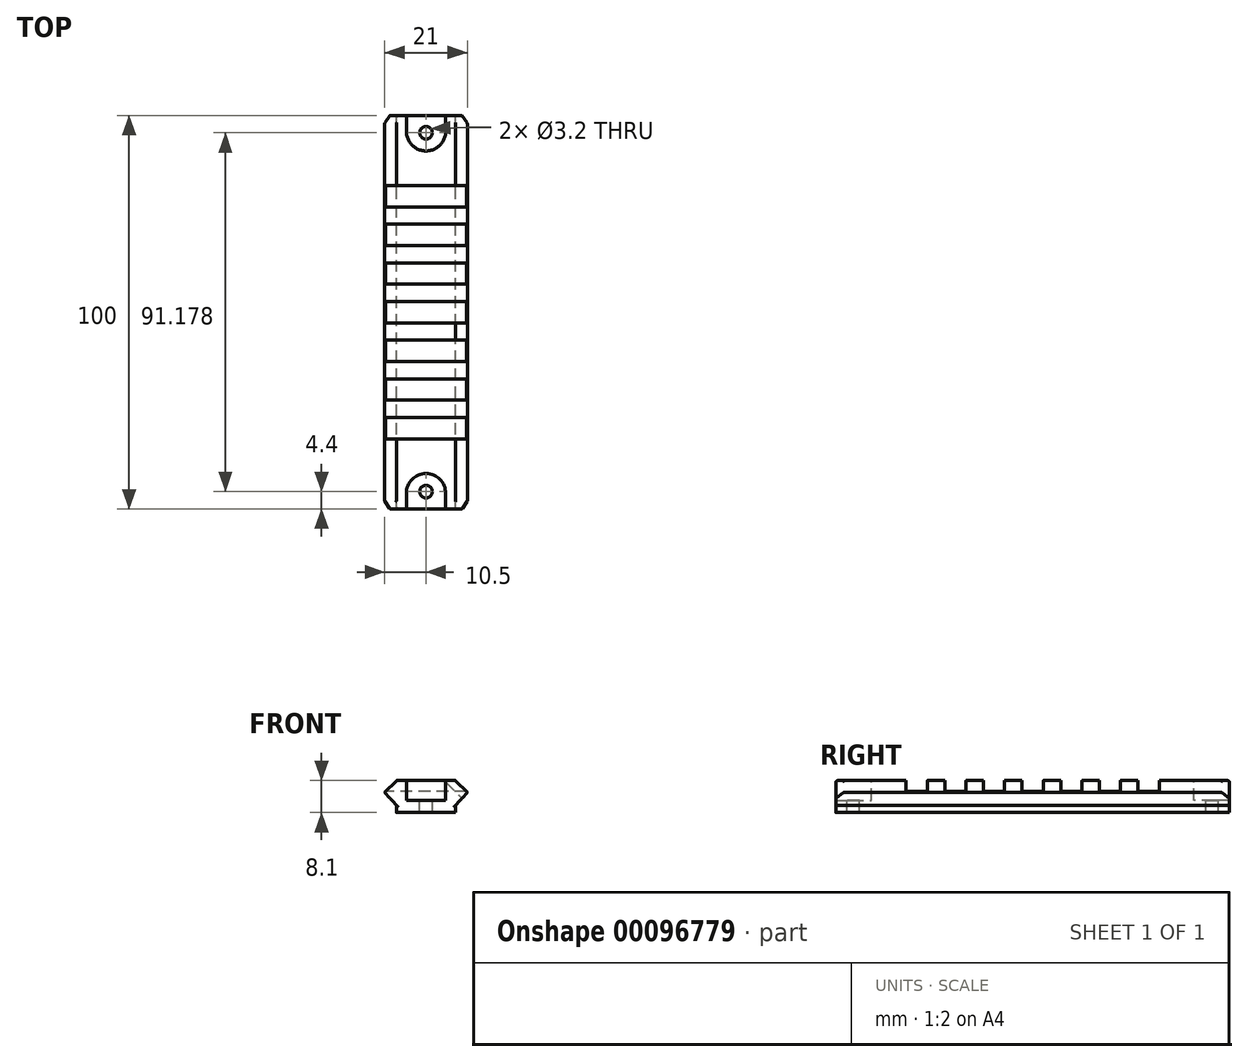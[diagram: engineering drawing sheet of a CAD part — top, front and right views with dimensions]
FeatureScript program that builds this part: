
annotation { "Feature Type Name" : "Feature", "Feature Type Description" : "" }
export const myFeature = defineFeature(function(context is Context, id is Id, definition is map)
    precondition{}
    {
        {
            var Q0;
            Q0=qCreatedBy(makeId("Front.planeOp"),FACE);
            var sketch = newSketch(context, id + "F0", { "sketchPlane" : qUnion([Q0])});
            skPoint(sketch, "E0", {"position": v(7.5, 0) * mm});
            skPoint(sketch, "E1", {"position": v(-7.5, 0) * mm});
            skPoint(sketch, "E2", {"position": v(0, 3.3) * mm});
            skPoint(sketch, "E3", {"position": v(0, -4.8) * mm});
            skLineSegment(sketch, "E4", {"start": v(7.5, -4.8) * mm, "end": v(-7.5, -4.8) * mm});
            skLineSegment(sketch, "E5", {"start": v(7.5, -4.8) * mm, "end": v(7.5, -3) * mm});
            skLineSegment(sketch, "E6", {"start": v(-7.5, -3) * mm, "end": v(-7.5, -4.8) * mm});
            skLineSegment(sketch, "E7", {"start": v(-7.5, -3) * mm, "end": v(-10.5, 0.3) * mm});
            skLineSegment(sketch, "E8", {"start": v(7.5, -3) * mm, "end": v(10.5, 0.3) * mm});
            skPoint(sketch, "E9", {"position": v(7.5, 3.3) * mm});
            skPoint(sketch, "E10", {"position": v(-7.5, 3.3) * mm});
            skLineSegment(sketch, "E11", {"start": v(-10.5, 0.3) * mm, "end": v(-7.5, 3.3) * mm});
            skLineSegment(sketch, "E12", {"start": v(10.5, 0.3) * mm, "end": v(7.5, 3.3) * mm});
            skLineSegment(sketch, "E13", {"start": v(-7.5, 3.3) * mm, "end": v(7.5, 3.3) * mm});
            skSolve(sketch);
        }
        {
            var Q0;
            Q0=qSketchRegion(id+"F0",true);
            extrude(context, id + "F1", {"entities" : qUnion([Q0]), "endBound" : BoundingType.SYMMETRIC, "depth" : 100 * mm});
        }
        {
            var Q0;
            Q0=makeQuery(id+"F1.opExtrude","SWEPT_FACE",FACE,{"disambiguationData":[OSD([sQuery(id+"F0.wireOp",EDGE,"E13")])]});
            var sketch = newSketch(context, id + "F2", { "sketchPlane" : qUnion([Q0])});
            skPoint(sketch, "E14", {"position": v(0, 2.7) * mm});
            skPoint(sketch, "E15", {"position": v(0, -2.7) * mm});
            skLineSegment(sketch, "E16", {"start": v(-14, -2.7) * mm, "end": v(14, -2.7) * mm});
            skLineSegment(sketch, "E17", {"start": v(14, -2.7) * mm, "end": v(14, 2.7) * mm});
            skLineSegment(sketch, "E18", {"start": v(14, 2.7) * mm, "end": v(-14, 2.7) * mm});
            skLineSegment(sketch, "E19", {"start": v(-14, -2.7) * mm, "end": v(-14, 2.7) * mm});
            skLineSegment(sketch, "E20", {"start": v(0, 50) * mm, "end": v(0, 35) * mm});
            skPoint(sketch, "E20.endSnap0", {"position": v(0, 50) * mm});
            skLineSegment(sketch, "E21.0.1.0", {"start": v(-14, 7.12) * mm, "end": v(-14.1, 12.52) * mm});
            skLineSegment(sketch, "E21.0.1.1", {"start": v(14.12, 12.52) * mm, "end": v(-14.1, 12.52) * mm});
            skLineSegment(sketch, "E21.0.1.2", {"start": v(-14, 7.12) * mm, "end": v(14.12, 7.12) * mm});
            skLineSegment(sketch, "E21.0.1.3", {"start": v(14.12, 7.12) * mm, "end": v(14.12, 12.52) * mm});
            skLineSegment(sketch, "E21.0.2.0", {"start": v(-13.81, 16.94) * mm, "end": v(-13.81, 22.34) * mm});
            skLineSegment(sketch, "E21.0.2.1", {"start": v(14.52, 22.34) * mm, "end": v(-13.81, 22.34) * mm});
            skLineSegment(sketch, "E21.0.2.2", {"start": v(-13.81, 16.94) * mm, "end": v(14.52, 16.94) * mm});
            skLineSegment(sketch, "E21.0.2.3", {"start": v(14.52, 16.94) * mm, "end": v(14.52, 22.34) * mm});
            skLineSegment(sketch, "E21.0.3.0", {"start": v(-14.12, 26.76) * mm, "end": v(-14.12, 32.16) * mm});
            skLineSegment(sketch, "E21.0.3.1", {"start": v(14.7, 32.16) * mm, "end": v(-14.12, 32.16) * mm});
            skLineSegment(sketch, "E21.0.3.2", {"start": v(-14.12, 26.76) * mm, "end": v(14.7, 26.76) * mm});
            skLineSegment(sketch, "E21.0.3.3", {"start": v(14.7, 26.76) * mm, "end": v(14.7, 32.16) * mm});
            skLineSegment(sketch, "E21.direction2", {"start": v(-14, -2.7) * mm, "end": v(-14, 7.12) * mm, "construction": true});
            skLineSegment(sketch, "E22.0.1.0", {"start": v(-13.9, -12.52) * mm, "end": v(14.62, -12.52) * mm});
            skLineSegment(sketch, "E22.0.1.1", {"start": v(-13.9, -12.52) * mm, "end": v(-13.9, -7.12) * mm});
            skLineSegment(sketch, "E22.0.1.2", {"start": v(14.62, -7.12) * mm, "end": v(-13.9, -7.12) * mm});
            skLineSegment(sketch, "E22.0.1.3", {"start": v(14.62, -12.52) * mm, "end": v(14.62, -7.12) * mm});
            skLineSegment(sketch, "E22.0.2.0", {"start": v(-14.68, -22.34) * mm, "end": v(14.93, -22.34) * mm});
            skLineSegment(sketch, "E22.0.2.1", {"start": v(-14.68, -22.34) * mm, "end": v(-14.68, -16.94) * mm});
            skLineSegment(sketch, "E22.0.2.2", {"start": v(14.93, -16.94) * mm, "end": v(-14.68, -16.94) * mm});
            skLineSegment(sketch, "E22.0.2.3", {"start": v(14.93, -22.34) * mm, "end": v(14.93, -16.94) * mm});
            skLineSegment(sketch, "E22.0.3.0", {"start": v(-14.78, -32.16) * mm, "end": v(15.13, -32.16) * mm});
            skLineSegment(sketch, "E22.0.3.1", {"start": v(-14.78, -32.16) * mm, "end": v(-14.78, -26.76) * mm});
            skLineSegment(sketch, "E22.0.3.2", {"start": v(15.13, -26.76) * mm, "end": v(-14.78, -26.76) * mm});
            skLineSegment(sketch, "E22.0.3.3", {"start": v(15.13, -32.16) * mm, "end": v(15.13, -26.76) * mm});
            skLineSegment(sketch, "E22.direction2", {"start": v(-14, -2.7) * mm, "end": v(-13.9, -12.52) * mm, "construction": true});
            skSolve(sketch);
        }
        {
            var Q0;
            Q0=qSketchRegion(id+"F2",true);
            extrude(context, id + "F3", {"entities" : qUnion([Q0]), "operationType" : NewBodyOperationType.REMOVE, "oppositeDirection" : true, "depth" : 2.8 * mm});
        }
        {
            var Q0;
            Q0=qCreatedBy(makeId("Top.planeOp"),FACE);
            var sketch = newSketch(context, id + "F4", { "sketchPlane" : qUnion([Q0])});
            skPoint(sketch, "E23", {"position": v(0, -50) * mm});
            skPoint(sketch, "E24", {"position": v(0, -48) * mm});
            skPoint(sketch, "E25", {"position": v(-11, -48.94) * mm});
            skPoint(sketch, "E26", {"position": v(-5, -48.94) * mm});
            skPoint(sketch, "E27", {"position": v(5, -48.94) * mm});
            skPoint(sketch, "E28", {"position": v(-5, -50) * mm});
            skPoint(sketch, "E29", {"position": v(5, -50) * mm});
            skLineSegment(sketch, "E30", {"start": v(-5, -48) * mm, "end": v(-5, -50) * mm});
            skLineSegment(sketch, "E31", {"start": v(-5, -48) * mm, "end": v(-5, -43) * mm});
            skLineSegment(sketch, "E32", {"start": v(5, -50) * mm, "end": v(5, -48) * mm});
            skLineSegment(sketch, "E33", {"start": v(5, -48) * mm, "end": v(5, -43) * mm});
            skArc(sketch, "E34", {"start": v(5, -43) * mm, "mid": v(0, -38) * mm, "end": v(-5, -43) * mm});
            skArc(sketch, "E35.MirrorCS", {"start": v(5, 43) * mm, "mid": v(0, 38) * mm, "end": v(-5, 43) * mm});
            skLineSegment(sketch, "E36.MirrorCS", {"start": v(-5, 48) * mm, "end": v(-5, 43) * mm});
            skLineSegment(sketch, "E37.MirrorCS", {"start": v(5, 48) * mm, "end": v(5, 43) * mm});
            skLineSegment(sketch, "E38.MirrorCS", {"start": v(5, 50) * mm, "end": v(5, 48) * mm});
            skLineSegment(sketch, "E39.MirrorCS", {"start": v(-5, 48) * mm, "end": v(-5, 50) * mm});
            skSolve(sketch);
        }
        {
            var Q0;
            {var subQ0=sQuery(id+"F0.wireOp",EDGE,"E13");Q0=makeQuery(id+"F3.boolean.opBoolean","SPLIT",FACE,{"disambiguationData":[TD([makeQuery(id+"F3.opExtrude","SWEPT_FACE",FACE,{"disambiguationData":[OSD([sQuery(id+"F2.wireOp",EDGE,"E22.0.3.0")])]})])],"derivedFrom":makeQuery(id+"F1.opExtrude","SWEPT_FACE",FACE,{"disambiguationData":[OSD([subQ0])]})});}
            var sketch = newSketch(context, id + "F5", { "sketchPlane" : qUnion([Q0])});
            skPoint(sketch, "E40", {"position": v(0, -50) * mm});
            skPoint(sketch, "E41", {"position": v(0, -48) * mm});
            skPoint(sketch, "E42", {"position": v(-11, -48.94) * mm});
            skPoint(sketch, "E43", {"position": v(-5, -48.94) * mm});
            skPoint(sketch, "E44", {"position": v(5, -48.94) * mm});
            skPoint(sketch, "E45", {"position": v(-5, -50) * mm});
            skPoint(sketch, "E46", {"position": v(5, -50) * mm});
            skLineSegment(sketch, "E47", {"start": v(-5, -48) * mm, "end": v(-5, -50) * mm});
            skLineSegment(sketch, "E48", {"start": v(-5, -48) * mm, "end": v(-5, -46) * mm});
            skLineSegment(sketch, "E49", {"start": v(5, -50) * mm, "end": v(5, -48) * mm});
            skLineSegment(sketch, "E50", {"start": v(5, -48) * mm, "end": v(5, -46) * mm});
            skArc(sketch, "E51", {"start": v(5, -46) * mm, "mid": v(0, -41) * mm, "end": v(-5, -46) * mm});
            skArc(sketch, "E52.MirrorCS", {"start": v(5, 46) * mm, "mid": v(0, 40.98) * mm, "end": v(-5, 46) * mm});
            skLineSegment(sketch, "E53.MirrorCS", {"start": v(-5, 48) * mm, "end": v(-5, 46) * mm});
            skLineSegment(sketch, "E54.MirrorCS", {"start": v(5, 48) * mm, "end": v(5, 46) * mm});
            skLineSegment(sketch, "E55.MirrorCS", {"start": v(5, 50) * mm, "end": v(5, 48) * mm});
            skLineSegment(sketch, "E56.MirrorCS", {"start": v(-5, 48) * mm, "end": v(-5, 50) * mm});
            skLineSegment(sketch, "E57", {"start": v(-5, -50) * mm, "end": v(5, -50) * mm});
            skLineSegment(sketch, "E58", {"start": v(-5, 50) * mm, "end": v(5, 50) * mm});
            skSolve(sketch);
        }
        {
            var Q0;
            Q0=qSketchRegion(id+"F5",true);
            extrude(context, id + "F6", {"entities" : qUnion([Q0]), "operationType" : NewBodyOperationType.REMOVE, "oppositeDirection" : true, "depth" : 5 * mm});
        }
        {
            var Q0;
            Q0=makeQuery(id+"F6.boolean.opBoolean","COPY",FACE,{"derivedFrom":makeQuery(id+"F6.opExtrude","CAP_FACE",FACE,{"disambiguationData":[OSD([sQuery(id+"F5.wireOp",EDGE,"E47"),sQuery(id+"F5.wireOp",EDGE,"E48"),sQuery(id+"F5.wireOp",EDGE,"E49"),sQuery(id+"F5.wireOp",EDGE,"E50"),sQuery(id+"F5.wireOp",EDGE,"E51"),sQuery(id+"F5.wireOp",EDGE,"E57")])],"isStart":false})});
            var sketch = newSketch(context, id + "F7", { "sketchPlane" : qUnion([Q0])});
            skCircle(sketch, "E59", {"center": v(0, -45.6) * mm, "radius": 1.6 * mm});
            skCircle(sketch, "E60", {"center": v(0, 45.58) * mm, "radius": 1.6 * mm});
            skSolve(sketch);
        }
        {
            var Q0;
            Q0=qSketchRegion(id+"F7",true);
            extrude(context, id + "F8", {"entities" : qUnion([Q0]), "operationType" : NewBodyOperationType.REMOVE, "endBound" : BoundingType.THROUGH_ALL, "oppositeDirection" : true, "depth" : 25 * mm});
        }
        {
            var Q0;
            Q0=makeQuery(id+"F1.opExtrude","CAP_EDGE",EDGE,{"disambiguationData":[OSD([sQuery(id+"F0.wireOp",EDGE,"E12")])],"isStart":true});
            var Q1;
            Q1=makeQuery(id+"F1.opExtrude","CAP_EDGE",EDGE,{"disambiguationData":[OSD([sQuery(id+"F0.wireOp",EDGE,"E11")])],"isStart":true});
            var Q2;
            Q2=makeQuery(id+"F1.opExtrude","CAP_EDGE",EDGE,{"disambiguationData":[OSD([sQuery(id+"F0.wireOp",EDGE,"E12")])],"isStart":false});
            var Q3;
            Q3=makeQuery(id+"F1.opExtrude","CAP_EDGE",EDGE,{"disambiguationData":[OSD([sQuery(id+"F0.wireOp",EDGE,"E11")])],"isStart":false});
            chamfer(context, id + "F9", {"entities" : qUnion([Q0, Q1, Q2, Q3]), "width" : 2 * mm, "tangentPropagation" : true});
        }
        {
            var Q0;
            {var subQ0=sQuery(id+"F0.wireOp",EDGE,"E11");var subQ1=sQuery(id+"F0.wireOp",EDGE,"E13");Q0=makeQuery(id+"F3.boolean.opBoolean","SPLIT",EDGE,{"disambiguationData":[TD([makeQuery(id+"F3.opExtrude","SWEPT_FACE",FACE,{"disambiguationData":[OSD([sQuery(id+"F2.wireOp",EDGE,"E21.0.2.1")])]})])],"derivedFrom":makeQuery(id+"F1.opExtrude","SWEPT_EDGE",EDGE,{"disambiguationData":[OSD([subQ0,subQ1])]})});}
            var Q1;
            {var subQ0=sQuery(id+"F0.wireOp",EDGE,"E11");var subQ1=sQuery(id+"F0.wireOp",EDGE,"E13");Q1=makeQuery(id+"F3.boolean.opBoolean","SPLIT",EDGE,{"disambiguationData":[TD([makeQuery(id+"F3.opExtrude","SWEPT_FACE",FACE,{"disambiguationData":[OSD([sQuery(id+"F2.wireOp",EDGE,"E21.0.1.1")])]})])],"derivedFrom":makeQuery(id+"F1.opExtrude","SWEPT_EDGE",EDGE,{"disambiguationData":[OSD([subQ0,subQ1])]})});}
            var Q2;
            {var subQ0=sQuery(id+"F0.wireOp",EDGE,"E11");var subQ1=sQuery(id+"F0.wireOp",EDGE,"E13");Q2=makeQuery(id+"F3.boolean.opBoolean","SPLIT",EDGE,{"disambiguationData":[TD([makeQuery(id+"F3.opExtrude","SWEPT_FACE",FACE,{"disambiguationData":[OSD([sQuery(id+"F2.wireOp",EDGE,"E18")])]})])],"derivedFrom":makeQuery(id+"F1.opExtrude","SWEPT_EDGE",EDGE,{"disambiguationData":[OSD([subQ0,subQ1])]})});}
            var Q3;
            {var subQ0=sQuery(id+"F0.wireOp",EDGE,"E11");var subQ1=sQuery(id+"F0.wireOp",EDGE,"E13");Q3=makeQuery(id+"F3.boolean.opBoolean","SPLIT",EDGE,{"disambiguationData":[TD([makeQuery(id+"F3.opExtrude","SWEPT_FACE",FACE,{"disambiguationData":[OSD([sQuery(id+"F2.wireOp",EDGE,"E16")])]})])],"derivedFrom":makeQuery(id+"F1.opExtrude","SWEPT_EDGE",EDGE,{"disambiguationData":[OSD([subQ0,subQ1])]})});}
            var Q4;
            {var subQ0=sQuery(id+"F0.wireOp",EDGE,"E11");var subQ1=sQuery(id+"F0.wireOp",EDGE,"E13");Q4=makeQuery(id+"F3.boolean.opBoolean","SPLIT",EDGE,{"disambiguationData":[TD([makeQuery(id+"F3.opExtrude","SWEPT_FACE",FACE,{"disambiguationData":[OSD([sQuery(id+"F2.wireOp",EDGE,"E22.0.1.0")])]})])],"derivedFrom":makeQuery(id+"F1.opExtrude","SWEPT_EDGE",EDGE,{"disambiguationData":[OSD([subQ0,subQ1])]})});}
            var Q5;
            {var subQ0=sQuery(id+"F0.wireOp",EDGE,"E11");var subQ1=sQuery(id+"F0.wireOp",EDGE,"E13");Q5=makeQuery(id+"F3.boolean.opBoolean","SPLIT",EDGE,{"disambiguationData":[TD([makeQuery(id+"F3.opExtrude","SWEPT_FACE",FACE,{"disambiguationData":[OSD([sQuery(id+"F2.wireOp",EDGE,"E22.0.2.0")])]})])],"derivedFrom":makeQuery(id+"F1.opExtrude","SWEPT_EDGE",EDGE,{"disambiguationData":[OSD([subQ0,subQ1])]})});}
            var Q6;
            {var subQ0=sQuery(id+"F0.wireOp",EDGE,"E12");var subQ1=sQuery(id+"F0.wireOp",EDGE,"E13");Q6=makeQuery(id+"F3.boolean.opBoolean","SPLIT",EDGE,{"disambiguationData":[TD([makeQuery(id+"F3.opExtrude","SWEPT_FACE",FACE,{"disambiguationData":[OSD([sQuery(id+"F2.wireOp",EDGE,"E22.0.2.0")])]})])],"derivedFrom":makeQuery(id+"F1.opExtrude","SWEPT_EDGE",EDGE,{"disambiguationData":[OSD([subQ0,subQ1])]})});}
            var Q7;
            {var subQ0=sQuery(id+"F0.wireOp",EDGE,"E12");var subQ1=sQuery(id+"F0.wireOp",EDGE,"E13");Q7=makeQuery(id+"F3.boolean.opBoolean","SPLIT",EDGE,{"disambiguationData":[TD([makeQuery(id+"F3.opExtrude","SWEPT_FACE",FACE,{"disambiguationData":[OSD([sQuery(id+"F2.wireOp",EDGE,"E22.0.1.0")])]})])],"derivedFrom":makeQuery(id+"F1.opExtrude","SWEPT_EDGE",EDGE,{"disambiguationData":[OSD([subQ0,subQ1])]})});}
            var Q8;
            {var subQ0=sQuery(id+"F0.wireOp",EDGE,"E12");var subQ1=sQuery(id+"F0.wireOp",EDGE,"E13");Q8=makeQuery(id+"F3.boolean.opBoolean","SPLIT",EDGE,{"disambiguationData":[TD([makeQuery(id+"F3.opExtrude","SWEPT_FACE",FACE,{"disambiguationData":[OSD([sQuery(id+"F2.wireOp",EDGE,"E18")])]})])],"derivedFrom":makeQuery(id+"F1.opExtrude","SWEPT_EDGE",EDGE,{"disambiguationData":[OSD([subQ0,subQ1])]})});}
            var Q9;
            {var subQ0=sQuery(id+"F0.wireOp",EDGE,"E12");var subQ1=sQuery(id+"F0.wireOp",EDGE,"E13");Q9=makeQuery(id+"F3.boolean.opBoolean","SPLIT",EDGE,{"disambiguationData":[TD([makeQuery(id+"F3.opExtrude","SWEPT_FACE",FACE,{"disambiguationData":[OSD([sQuery(id+"F2.wireOp",EDGE,"E21.0.1.1")])]})])],"derivedFrom":makeQuery(id+"F1.opExtrude","SWEPT_EDGE",EDGE,{"disambiguationData":[OSD([subQ0,subQ1])]})});}
            var Q10;
            {var subQ0=sQuery(id+"F0.wireOp",EDGE,"E12");var subQ1=sQuery(id+"F0.wireOp",EDGE,"E13");Q10=makeQuery(id+"F3.boolean.opBoolean","SPLIT",EDGE,{"disambiguationData":[TD([makeQuery(id+"F3.opExtrude","SWEPT_FACE",FACE,{"disambiguationData":[OSD([sQuery(id+"F2.wireOp",EDGE,"E21.0.2.1")])]})])],"derivedFrom":makeQuery(id+"F1.opExtrude","SWEPT_EDGE",EDGE,{"disambiguationData":[OSD([subQ0,subQ1])]})});}
            var Q11;
            {var subQ0=sQuery(id+"F0.wireOp",EDGE,"E13");var subQ2=sQuery(id+"F0.wireOp",EDGE,"E11");Q11=makeQuery(id+"F9.opChamfer","BLEND_EDGE",EDGE,{"blendedFrom":[makeQuery(id+"F1.opExtrude","CAP_EDGE",EDGE,{"disambiguationData":[OSD([subQ2])],"isStart":true}),makeQuery(id+"F3.boolean.opBoolean","SPLIT",FACE,{"disambiguationData":[TD([makeQuery(id+"F3.opExtrude","SWEPT_FACE",FACE,{"disambiguationData":[OSD([sQuery(id+"F2.wireOp",EDGE,"E21.0.3.1")])]})])],"derivedFrom":makeQuery(id+"F1.opExtrude","SWEPT_FACE",FACE,{"disambiguationData":[OSD([subQ0])]})})],"blendedInto":[makeQuery(id+"F3.boolean.opBoolean","SPLIT",FACE,{"disambiguationData":[TD([makeQuery(id+"F3.opExtrude","SWEPT_FACE",FACE,{"disambiguationData":[OSD([sQuery(id+"F2.wireOp",EDGE,"E21.0.3.1")])]})])],"derivedFrom":makeQuery(id+"F1.opExtrude","SWEPT_FACE",FACE,{"disambiguationData":[OSD([subQ0])]})})]});}
            var Q12;
            {var subQ0=sQuery(id+"F0.wireOp",EDGE,"E11");Q12=makeQuery(id+"F9.opChamfer","BLEND_EDGE",EDGE,{"blendedFrom":[makeQuery(id+"F1.opExtrude","CAP_EDGE",EDGE,{"disambiguationData":[OSD([subQ0])],"isStart":true}),makeQuery(id+"F1.opExtrude","CAP_FACE",FACE,{"disambiguationData":[OSD([sQuery(id+"F0.wireOp",EDGE,"E4"),sQuery(id+"F0.wireOp",EDGE,"E5"),sQuery(id+"F0.wireOp",EDGE,"E6"),sQuery(id+"F0.wireOp",EDGE,"E7"),sQuery(id+"F0.wireOp",EDGE,"E8"),subQ0,sQuery(id+"F0.wireOp",EDGE,"E12"),sQuery(id+"F0.wireOp",EDGE,"E13")])],"isStart":true})],"blendedInto":[makeQuery(id+"F1.opExtrude","CAP_FACE",FACE,{"disambiguationData":[OSD([sQuery(id+"F0.wireOp",EDGE,"E4"),sQuery(id+"F0.wireOp",EDGE,"E5"),sQuery(id+"F0.wireOp",EDGE,"E6"),sQuery(id+"F0.wireOp",EDGE,"E7"),sQuery(id+"F0.wireOp",EDGE,"E8"),subQ0,sQuery(id+"F0.wireOp",EDGE,"E12"),sQuery(id+"F0.wireOp",EDGE,"E13")])],"isStart":true})]});}
            var Q13;
            {var subQ0=sQuery(id+"F0.wireOp",EDGE,"E13");var subQ1=sQuery(id+"F0.wireOp",EDGE,"E12");Q13=makeQuery(id+"F9.opChamfer","BLEND_EDGE",EDGE,{"blendedFrom":[makeQuery(id+"F1.opExtrude","CAP_EDGE",EDGE,{"disambiguationData":[OSD([subQ1])],"isStart":true}),makeQuery(id+"F3.boolean.opBoolean","SPLIT",FACE,{"disambiguationData":[TD([makeQuery(id+"F3.opExtrude","SWEPT_FACE",FACE,{"disambiguationData":[OSD([sQuery(id+"F2.wireOp",EDGE,"E21.0.3.1")])]})])],"derivedFrom":makeQuery(id+"F1.opExtrude","SWEPT_FACE",FACE,{"disambiguationData":[OSD([subQ0])]})})],"blendedInto":[makeQuery(id+"F3.boolean.opBoolean","SPLIT",FACE,{"disambiguationData":[TD([makeQuery(id+"F3.opExtrude","SWEPT_FACE",FACE,{"disambiguationData":[OSD([sQuery(id+"F2.wireOp",EDGE,"E21.0.3.1")])]})])],"derivedFrom":makeQuery(id+"F1.opExtrude","SWEPT_FACE",FACE,{"disambiguationData":[OSD([subQ0])]})})]});}
            var Q14;
            {var subQ0=sQuery(id+"F0.wireOp",EDGE,"E12");Q14=makeQuery(id+"F9.opChamfer","BLEND_EDGE",EDGE,{"blendedFrom":[makeQuery(id+"F1.opExtrude","CAP_EDGE",EDGE,{"disambiguationData":[OSD([subQ0])],"isStart":true}),makeQuery(id+"F1.opExtrude","SWEPT_FACE",FACE,{"disambiguationData":[OSD([subQ0])]})],"blendedInto":[makeQuery(id+"F1.opExtrude","SWEPT_FACE",FACE,{"disambiguationData":[OSD([subQ0])]})]});}
            var Q15;
            {var subQ0=sQuery(id+"F0.wireOp",EDGE,"E11");Q15=makeQuery(id+"F9.opChamfer","BLEND_EDGE",EDGE,{"blendedFrom":[makeQuery(id+"F1.opExtrude","CAP_EDGE",EDGE,{"disambiguationData":[OSD([subQ0])],"isStart":true}),makeQuery(id+"F1.opExtrude","SWEPT_FACE",FACE,{"disambiguationData":[OSD([subQ0])]})],"blendedInto":[makeQuery(id+"F1.opExtrude","SWEPT_FACE",FACE,{"disambiguationData":[OSD([subQ0])]})]});}
            var Q16;
            {var subQ0=sQuery(id+"F0.wireOp",EDGE,"E12");Q16=makeQuery(id+"F9.opChamfer","BLEND_EDGE",EDGE,{"blendedFrom":[makeQuery(id+"F1.opExtrude","CAP_EDGE",EDGE,{"disambiguationData":[OSD([subQ0])],"isStart":false}),makeQuery(id+"F1.opExtrude","CAP_FACE",FACE,{"disambiguationData":[OSD([sQuery(id+"F0.wireOp",EDGE,"E4"),sQuery(id+"F0.wireOp",EDGE,"E5"),sQuery(id+"F0.wireOp",EDGE,"E6"),sQuery(id+"F0.wireOp",EDGE,"E7"),sQuery(id+"F0.wireOp",EDGE,"E8"),sQuery(id+"F0.wireOp",EDGE,"E11"),subQ0,sQuery(id+"F0.wireOp",EDGE,"E13")])],"isStart":false})],"blendedInto":[makeQuery(id+"F1.opExtrude","CAP_FACE",FACE,{"disambiguationData":[OSD([sQuery(id+"F0.wireOp",EDGE,"E4"),sQuery(id+"F0.wireOp",EDGE,"E5"),sQuery(id+"F0.wireOp",EDGE,"E6"),sQuery(id+"F0.wireOp",EDGE,"E7"),sQuery(id+"F0.wireOp",EDGE,"E8"),sQuery(id+"F0.wireOp",EDGE,"E11"),subQ0,sQuery(id+"F0.wireOp",EDGE,"E13")])],"isStart":false})]});}
            var Q17;
            {var subQ0=sQuery(id+"F0.wireOp",EDGE,"E12");Q17=makeQuery(id+"F9.opChamfer","BLEND_EDGE",EDGE,{"blendedFrom":[makeQuery(id+"F1.opExtrude","CAP_EDGE",EDGE,{"disambiguationData":[OSD([subQ0])],"isStart":false}),makeQuery(id+"F1.opExtrude","SWEPT_FACE",FACE,{"disambiguationData":[OSD([subQ0])]})],"blendedInto":[makeQuery(id+"F1.opExtrude","SWEPT_FACE",FACE,{"disambiguationData":[OSD([subQ0])]})]});}
            var Q18;
            {var subQ0=sQuery(id+"F0.wireOp",EDGE,"E13");var subQ1=sQuery(id+"F0.wireOp",EDGE,"E12");Q18=makeQuery(id+"F9.opChamfer","BLEND_EDGE",EDGE,{"blendedFrom":[makeQuery(id+"F1.opExtrude","CAP_EDGE",EDGE,{"disambiguationData":[OSD([subQ1])],"isStart":false}),makeQuery(id+"F3.boolean.opBoolean","SPLIT",FACE,{"disambiguationData":[TD([makeQuery(id+"F3.opExtrude","SWEPT_FACE",FACE,{"disambiguationData":[OSD([sQuery(id+"F2.wireOp",EDGE,"E22.0.3.0")])]})])],"derivedFrom":makeQuery(id+"F1.opExtrude","SWEPT_FACE",FACE,{"disambiguationData":[OSD([subQ0])]})})],"blendedInto":[makeQuery(id+"F3.boolean.opBoolean","SPLIT",FACE,{"disambiguationData":[TD([makeQuery(id+"F3.opExtrude","SWEPT_FACE",FACE,{"disambiguationData":[OSD([sQuery(id+"F2.wireOp",EDGE,"E22.0.3.0")])]})])],"derivedFrom":makeQuery(id+"F1.opExtrude","SWEPT_FACE",FACE,{"disambiguationData":[OSD([subQ0])]})})]});}
            var Q19;
            {var subQ0=sQuery(id+"F0.wireOp",EDGE,"E11");Q19=makeQuery(id+"F9.opChamfer","BLEND_EDGE",EDGE,{"blendedFrom":[makeQuery(id+"F1.opExtrude","CAP_EDGE",EDGE,{"disambiguationData":[OSD([subQ0])],"isStart":false}),makeQuery(id+"F1.opExtrude","CAP_FACE",FACE,{"disambiguationData":[OSD([sQuery(id+"F0.wireOp",EDGE,"E4"),sQuery(id+"F0.wireOp",EDGE,"E5"),sQuery(id+"F0.wireOp",EDGE,"E6"),sQuery(id+"F0.wireOp",EDGE,"E7"),sQuery(id+"F0.wireOp",EDGE,"E8"),subQ0,sQuery(id+"F0.wireOp",EDGE,"E12"),sQuery(id+"F0.wireOp",EDGE,"E13")])],"isStart":false})],"blendedInto":[makeQuery(id+"F1.opExtrude","CAP_FACE",FACE,{"disambiguationData":[OSD([sQuery(id+"F0.wireOp",EDGE,"E4"),sQuery(id+"F0.wireOp",EDGE,"E5"),sQuery(id+"F0.wireOp",EDGE,"E6"),sQuery(id+"F0.wireOp",EDGE,"E7"),sQuery(id+"F0.wireOp",EDGE,"E8"),subQ0,sQuery(id+"F0.wireOp",EDGE,"E12"),sQuery(id+"F0.wireOp",EDGE,"E13")])],"isStart":false})]});}
            var Q20;
            {var subQ0=sQuery(id+"F0.wireOp",EDGE,"E13");var subQ2=sQuery(id+"F0.wireOp",EDGE,"E11");Q20=makeQuery(id+"F9.opChamfer","BLEND_EDGE",EDGE,{"blendedFrom":[makeQuery(id+"F1.opExtrude","CAP_EDGE",EDGE,{"disambiguationData":[OSD([subQ2])],"isStart":false}),makeQuery(id+"F3.boolean.opBoolean","SPLIT",FACE,{"disambiguationData":[TD([makeQuery(id+"F3.opExtrude","SWEPT_FACE",FACE,{"disambiguationData":[OSD([sQuery(id+"F2.wireOp",EDGE,"E22.0.3.0")])]})])],"derivedFrom":makeQuery(id+"F1.opExtrude","SWEPT_FACE",FACE,{"disambiguationData":[OSD([subQ0])]})})],"blendedInto":[makeQuery(id+"F3.boolean.opBoolean","SPLIT",FACE,{"disambiguationData":[TD([makeQuery(id+"F3.opExtrude","SWEPT_FACE",FACE,{"disambiguationData":[OSD([sQuery(id+"F2.wireOp",EDGE,"E22.0.3.0")])]})])],"derivedFrom":makeQuery(id+"F1.opExtrude","SWEPT_FACE",FACE,{"disambiguationData":[OSD([subQ0])]})})]});}
            var Q21;
            {var subQ0=sQuery(id+"F0.wireOp",EDGE,"E11");Q21=makeQuery(id+"F9.opChamfer","BLEND_EDGE",EDGE,{"blendedFrom":[makeQuery(id+"F1.opExtrude","CAP_EDGE",EDGE,{"disambiguationData":[OSD([subQ0])],"isStart":false}),makeQuery(id+"F1.opExtrude","SWEPT_FACE",FACE,{"disambiguationData":[OSD([subQ0])]})],"blendedInto":[makeQuery(id+"F1.opExtrude","SWEPT_FACE",FACE,{"disambiguationData":[OSD([subQ0])]})]});}
            var Q22;
            Q22=makeQuery(id+"F1.opExtrude","CAP_EDGE",EDGE,{"disambiguationData":[OSD([sQuery(id+"F0.wireOp",EDGE,"E6")])],"isStart":false});
            var Q23;
            Q23=makeQuery(id+"F1.opExtrude","CAP_EDGE",EDGE,{"disambiguationData":[OSD([sQuery(id+"F0.wireOp",EDGE,"E5")])],"isStart":false});
            var Q24;
            Q24=makeQuery(id+"F1.opExtrude","CAP_EDGE",EDGE,{"disambiguationData":[OSD([sQuery(id+"F0.wireOp",EDGE,"E5")])],"isStart":true});
            var Q25;
            Q25=makeQuery(id+"F1.opExtrude","CAP_EDGE",EDGE,{"disambiguationData":[OSD([sQuery(id+"F0.wireOp",EDGE,"E6")])],"isStart":true});
            fillet(context, id + "F10", {"entities" : qUnion([Q0, Q1, Q2, Q3, Q4, Q5, Q6, Q7, Q8, Q9, Q10, Q11, Q12, Q13, Q14, Q15, Q16, Q17, Q18, Q19, Q20, Q21, Q22, Q23, Q24, Q25]), "radius" : 0.5 * mm, "tangentPropagation" : true, "allowEdgeOverflow" : false});
        }
    });
